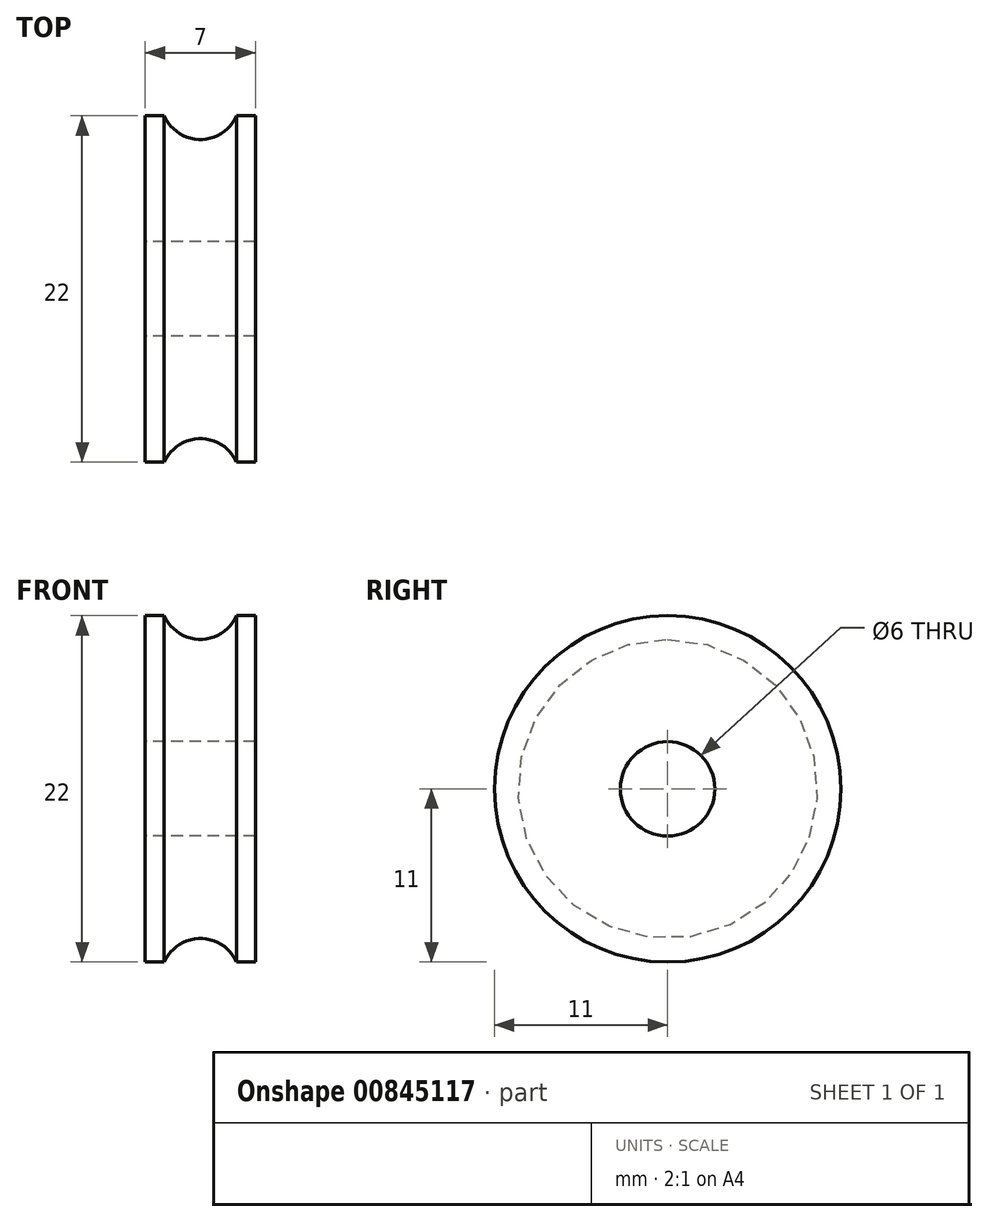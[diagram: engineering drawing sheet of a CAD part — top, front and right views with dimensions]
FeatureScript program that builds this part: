
annotation { "Feature Type Name" : "Feature", "Feature Type Description" : "" }
export const myFeature = defineFeature(function(context is Context, id is Id, definition is map)
    precondition{}
    {
        {
            var Q0;
            Q0=qCreatedBy(makeId("Right.planeOp"),FACE);
            var sketch = newSketch(context, id + "F0", { "sketchPlane" : qUnion([Q0])});
            skCircle(sketch, "E0", {"center": v(0, 0) * mm, "radius": 11 * mm});
            skSolve(sketch);
        }
        {
            var Q0;
            Q0 = qSketchRegion(id + "F0", true);
            extrude(context, id + "F1", {"entities" : qUnion([Q0]), "depth" : 3.5 * mm, "offsetDistance" : 25 * mm, "hasSecondDirection" : true, "secondDirectionOppositeDirection" : true, "secondDirectionDepth" : 3.5 * mm});
        }
        {
            var Q0;
            Q0=qCreatedBy(makeId("Front.planeOp"),FACE);
            var sketch = newSketch(context, id + "F2", { "sketchPlane" : qUnion([Q0])});
            skCircle(sketch, "E1", {"center": v(0, 12) * mm, "radius": 2.5 * mm});
            skLineSegment(sketch, "E2", {"start": v(0, 0) * mm, "end": v(-10, 0) * mm, "construction": true});
            skSolve(sketch);
        }
        {
            var Q0;
            Q0=makeQuery(id+"F2.imprint","IMPRINT",FACE,{"disambiguationData":[TD([[makeQuery(id+"F2.imprint","IMPRINT",EDGE,{"derivedFrom":sQuery(id+"F2.wireOp",EDGE,"E1")}),1.0]])]});
            var Q1;
            Q1=sQuery(id+"F2.wireOp",EDGE,"E2");
            revolve(context, id + "F3", {"operationType" : NewBodyOperationType.REMOVE, "surfaceOperationType" : NewSurfaceOperationType.NEW, "entities" : qUnion([Q0]), "axis" : qUnion([Q1]), "revolveType" : RevolveType.FULL, "oppositeDirection" : true});
        }
        {
            var Q0;
            Q0=makeQuery(id+"F1.opExtrude","CAP_FACE",FACE,{"disambiguationData":[OSD([sQuery(id+"F0.wireOp",EDGE,"E0")])],"isStart":true});
            var sketch = newSketch(context, id + "F4", { "sketchPlane" : qUnion([Q0])});
            skCircle(sketch, "E3", {"center": v(0, 0) * mm, "radius": 3 * mm});
            skSolve(sketch);
        }
        {
            var Q0;
            Q0 = qSketchRegion(id + "F4", true);
            extrude(context, id + "F5", {"entities" : qUnion([Q0]), "operationType" : NewBodyOperationType.REMOVE, "endBound" : BoundingType.UP_TO_NEXT, "oppositeDirection" : true, "depth" : 25 * mm, "offsetDistance" : 25 * mm});
        }
    });
